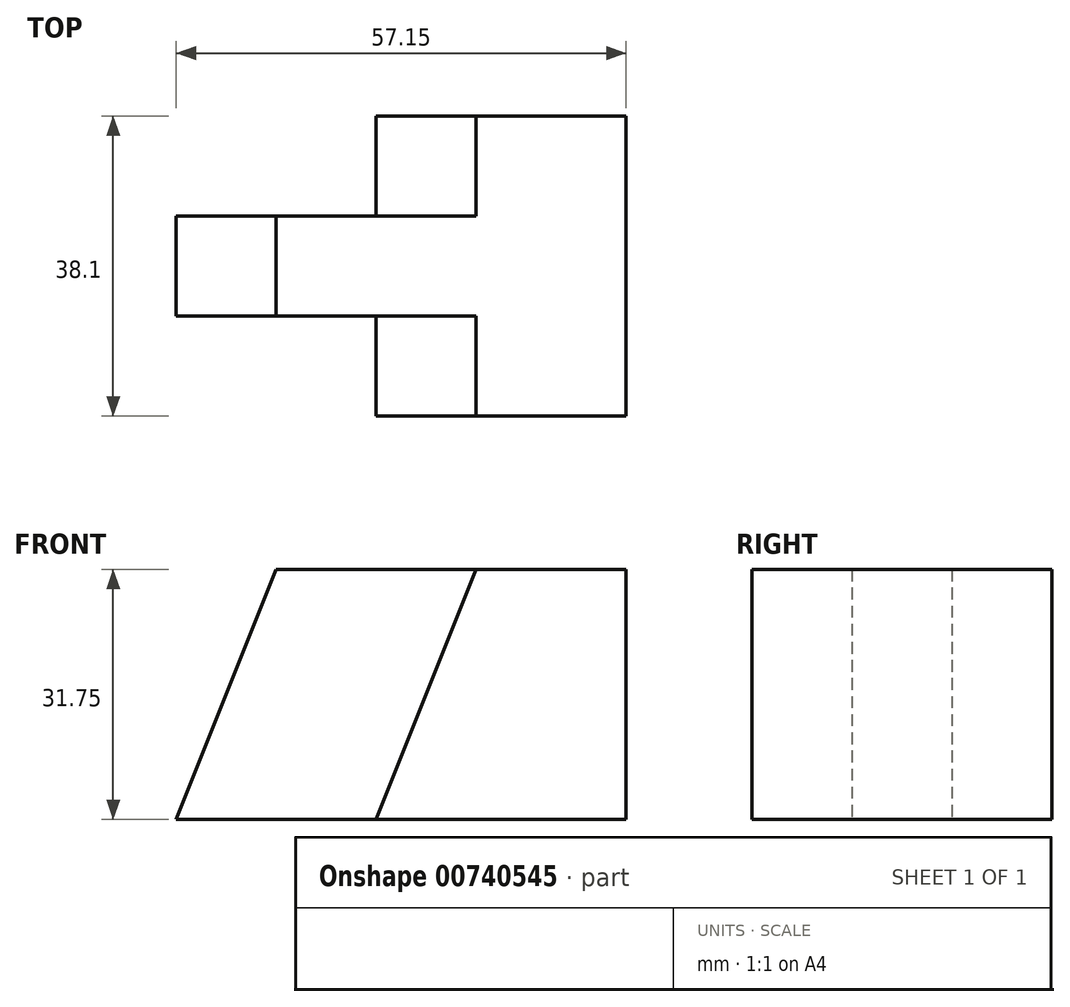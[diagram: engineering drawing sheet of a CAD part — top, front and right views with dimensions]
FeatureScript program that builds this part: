
annotation { "Feature Type Name" : "Feature", "Feature Type Description" : "" }
export const myFeature = defineFeature(function(context is Context, id is Id, definition is map)
    precondition{}
    {
        {
            var Q0;
            Q0=qCreatedBy(makeId("Front.planeOp"),FACE);
            var sketch = newSketch(context, id + "F0", { "sketchPlane" : qUnion([Q0])});
            skLineSegment(sketch, "E0", {"start": v(0, 0) * mm, "end": v(31.75, 0) * mm});
            skLineSegment(sketch, "E1", {"start": v(31.75, 0) * mm, "end": v(31.75, 31.75) * mm});
            skLineSegment(sketch, "E2", {"start": v(31.75, 31.75) * mm, "end": v(0, 31.75) * mm});
            skLineSegment(sketch, "E3", {"start": v(0, 31.75) * mm, "end": v(0, 0) * mm});
            skSolve(sketch);
        }
        {
            var Q0;
            Q0=makeQuery(id+"F0.imprint","IMPRINT",FACE,{"disambiguationData":[TD([[makeQuery(id+"F0.imprint","IMPRINT",EDGE,{"derivedFrom":sQuery(id+"F0.wireOp",EDGE,"E0")}),1.0]])]});
            extrude(context, id + "F1", {"entities" : qUnion([Q0]), "depth" : 38.1 * mm, "offsetDistance" : 25.4 * mm});
        }
        {
            var Q0;
            Q0 = qSketchRegion(id + "F0", true);
            extrude(context, id + "F2", {"entities" : qUnion([Q0]), "operationType" : NewBodyOperationType.ADD, "depth" : 25.4 * mm, "offsetDistance" : 25.4 * mm});
        }
        {
            var Q0;
            Q0=makeQuery(id+"F1.opExtrude","SWEPT_FACE",FACE,{"disambiguationData":[OSD([sQuery(id+"F0.wireOp",EDGE,"E3")])]});
            var sketch = newSketch(context, id + "F3", { "sketchPlane" : qUnion([Q0])});
            skLineSegment(sketch, "E4", {"start": v(12.7, 31.75) * mm, "end": v(12.7, 0) * mm});
            skLineSegment(sketch, "E5", {"start": v(12.7, 0) * mm, "end": v(25.4, 0) * mm});
            skLineSegment(sketch, "E6", {"start": v(25.4, 0) * mm, "end": v(25.4, 31.75) * mm});
            skLineSegment(sketch, "E7", {"start": v(25.4, 31.75) * mm, "end": v(12.7, 31.75) * mm});
            skSolve(sketch);
        }
        {
            var Q0;
            Q0 = qSketchRegion(id + "F3", true);
            extrude(context, id + "F4", {"entities" : qUnion([Q0]), "operationType" : NewBodyOperationType.ADD, "depth" : 25.4 * mm, "offsetDistance" : 25.4 * mm});
        }
        {
            var Q0;
            Q0=makeQuery(id+"F1.opExtrude","CAP_FACE",FACE,{"disambiguationData":[OSD([sQuery(id+"F0.wireOp",EDGE,"E0"),sQuery(id+"F0.wireOp",EDGE,"E1"),sQuery(id+"F0.wireOp",EDGE,"E2"),sQuery(id+"F0.wireOp",EDGE,"E3")])],"isStart":true});
            var sketch = newSketch(context, id + "F5", { "sketchPlane" : qUnion([Q0])});
            skLineSegment(sketch, "E8", {"start": v(0, 0) * mm, "end": v(-12.7, 31.75) * mm});
            skSolve(sketch);
        }
        {
            var Q0;
            Q0 = qSketchRegion(id + "F5", true);
            var Q1;
            {var subQ0=sQuery(id+"F5.wireOp",EDGE,"E8");Q1=makeQuery(id+"F5.imprint","IMPRINT",FACE,{"disambiguationData":[TD([[makeQuery(id+"F5.imprint","IMPRINT",EDGE,{"derivedFrom":subQ0}),-1.0]])]});}
            extrude(context, id + "F6", {"entities" : qUnion([Q0, Q1]), "operationType" : NewBodyOperationType.REMOVE, "oppositeDirection" : true, "depth" : 12.7 * mm, "offsetDistance" : 25.4 * mm});
        }
        {
            var Q0;
            Q0=makeQuery(id+"F1.opExtrude","CAP_FACE",FACE,{"disambiguationData":[OSD([sQuery(id+"F0.wireOp",EDGE,"E0"),sQuery(id+"F0.wireOp",EDGE,"E1"),sQuery(id+"F0.wireOp",EDGE,"E2"),sQuery(id+"F0.wireOp",EDGE,"E3")])],"isStart":false});
            var sketch = newSketch(context, id + "F7", { "sketchPlane" : qUnion([Q0])});
            skLineSegment(sketch, "E9", {"start": v(12.7, 31.75) * mm, "end": v(0, 0) * mm});
            skSolve(sketch);
        }
        {
            var Q0;
            {var subQ0=sQuery(id+"F7.wireOp",EDGE,"E9");Q0=makeQuery(id+"F7.imprint","IMPRINT",FACE,{"disambiguationData":[TD([[makeQuery(id+"F7.imprint","IMPRINT",EDGE,{"derivedFrom":subQ0}),-1.0]])]});}
            extrude(context, id + "F8", {"entities" : qUnion([Q0]), "operationType" : NewBodyOperationType.REMOVE, "oppositeDirection" : true, "depth" : 12.7 * mm, "offsetDistance" : 25.4 * mm});
        }
        {
            var Q0;
            Q0=makeQuery(id+"F6.boolean.opBoolean","MERGE",FACE,{"derivedFrom":[makeQuery(id+"F4.opExtrude","SWEPT_FACE",FACE,{"disambiguationData":[OSD([sQuery(id+"F3.wireOp",EDGE,"E4")])]}),makeQuery(id+"F6.opExtrude","CAP_FACE",FACE,{"disambiguationData":[OSD([sQuery(id+"F0.wireOp",EDGE,"E2"),sQuery(id+"F0.wireOp",EDGE,"E3"),sQuery(id+"F5.wireOp",EDGE,"E8")])],"isStart":false})]});
            var sketch = newSketch(context, id + "F9", { "sketchPlane" : qUnion([Q0])});
            skLineSegment(sketch, "E10", {"start": v(12.7, 31.75) * mm, "end": v(25.4, 0) * mm});
            skSolve(sketch);
        }
        {
            var Q0;
            {var subQ0=sQuery(id+"F9.wireOp",EDGE,"E10");Q0=makeQuery(id+"F9.imprint","IMPRINT",FACE,{"disambiguationData":[TD([[makeQuery(id+"F9.imprint","IMPRINT",EDGE,{"derivedFrom":subQ0}),1.0]])]});}
            extrude(context, id + "F10", {"entities" : qUnion([Q0]), "operationType" : NewBodyOperationType.REMOVE, "endBound" : BoundingType.THROUGH_ALL, "oppositeDirection" : true, "depth" : 25.4 * mm, "offsetDistance" : 25.4 * mm});
        }
    });
